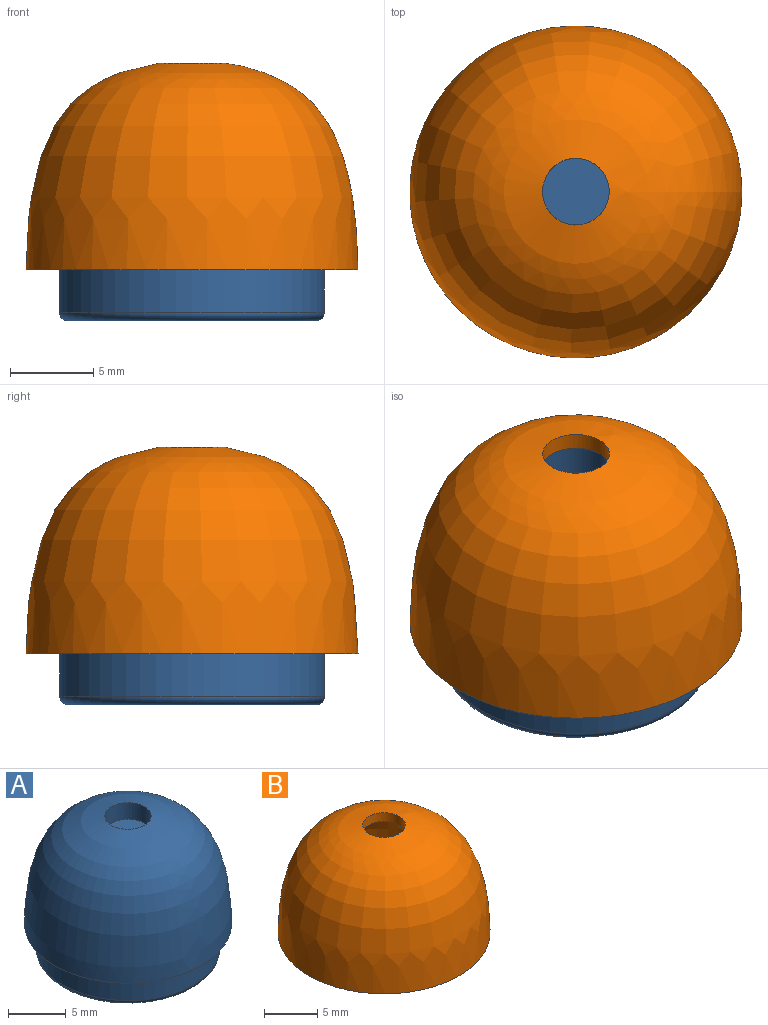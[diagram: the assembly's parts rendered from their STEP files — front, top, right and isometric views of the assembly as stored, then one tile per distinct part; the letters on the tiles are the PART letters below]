
ASSEMBLY  parts=2 mates=1
PART A: 11 faces, bbox 18x18x14.5 mm
  f0: plane 5x5mm, normal (0,0,-1), area 19.6mm2, adj f8
  f1: revolved ~18x18mm, area 1310.5mm2, adj f2,f9
  f2: plane 18x18mm, normal (0,0,-1), area 54.4mm2, adj f1,f3
  f3: cylinder r=7.98mm len=15.96mm, axis (0,0,1), area 129.1mm2, adj f2,f4
  f4: torus R=7.48mm, axis (0,0,1), area 38.5mm2, adj f3,f5
  f5: plane 14.96x14.96mm, normal (0,0,-1), area 37.5mm2, adj f4,f6
  f6: revolved ~14x14mm, area 134.2mm2, adj f5,f7
  f7: revolved ~14x14mm, area 411.2mm2, adj f6,f8
  f8: cylinder r=2.5mm len=5mm, axis (0,0,1), area 13.2mm2, adj f0,f7
  f9: cylinder r=2.01mm len=4.02mm, axis (0,0,1), area 22.3mm2, adj f1,f10
  f10: plane 4.02x4.02mm, normal (0,0,1), area 12.7mm2, adj f9
PART B: 4 faces, bbox 20x20x12.4 mm
  f0: revolved ~20x20mm, area 792.5mm2, adj f1,f3
  f1: plane 20x20mm, normal (0,0,-1), area 59.7mm2, adj f0,f2
  f2: revolved ~18x18mm, area 655.2mm2, adj f1,f3
  f3: cylinder r=2.01mm len=4.02mm, axis (0,0,1), area 12.7mm2, adj f0,f2
PLACE A t=(9.21,7.92,-0.32)mm
PLACE B rot(axis=(-1,0,0),0deg) t=(9.21,7.92,-0.32)mm
MATE fastened B.f3 <-> A.f4  axis (0,0,1) through (9.21,7.92,-0.32)mm
